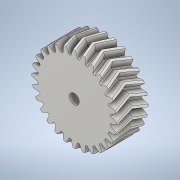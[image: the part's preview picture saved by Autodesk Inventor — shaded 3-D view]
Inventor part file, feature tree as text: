
AUTODESK INVENTOR PART (.ipt)
format: ipt  version: 2020 (Build 240168000, 168)  size: 722,432 bytes
history: native  units: mm (DEFAULTED — no unit token found)
features: plane x3, other x3, sketch x3, extrude x2, mirror x1
ambient origin geometry x8: Origin, YZ Plane, XZ Plane, XY Plane, X Axis, Y Axis, Z Axis, Center Point
bodies: Solid1 (feature_tree)
feature tree (12):
  extrude  "Extrusion1"  Depth=5.0mm TaperAngle=0.0deg
  plane  "Work Plane2"
  plane  "Work Plane8"
  plane  "Work Plane9"
  other  "Spur Gear"
  mirror  "Mirror2"
  extrude  "Extrusion3"  Depth=10.0mm TaperAngle=0.0deg
  sketch  "Sketch1"  dims[d0=27.133641mm d1=5.0mm d2=0.0mm]
  sketch  "Sketch2"  dims[d3=25.454545mm d4=10.0mm d5=0.0mm]
  other  "Srf1"
  sketch  "Sketch4"  dims[d16=25.0mm d17=0.0mm d34=1.121997mm d39=0.0mm d41=0.0mm d43=25.0mm d46=25.0mm d47=0.0mm d48=0.0mm d52=3.2mm d53=10.0mm d54=0.0mm]
  other  "Pitch Diameter"
